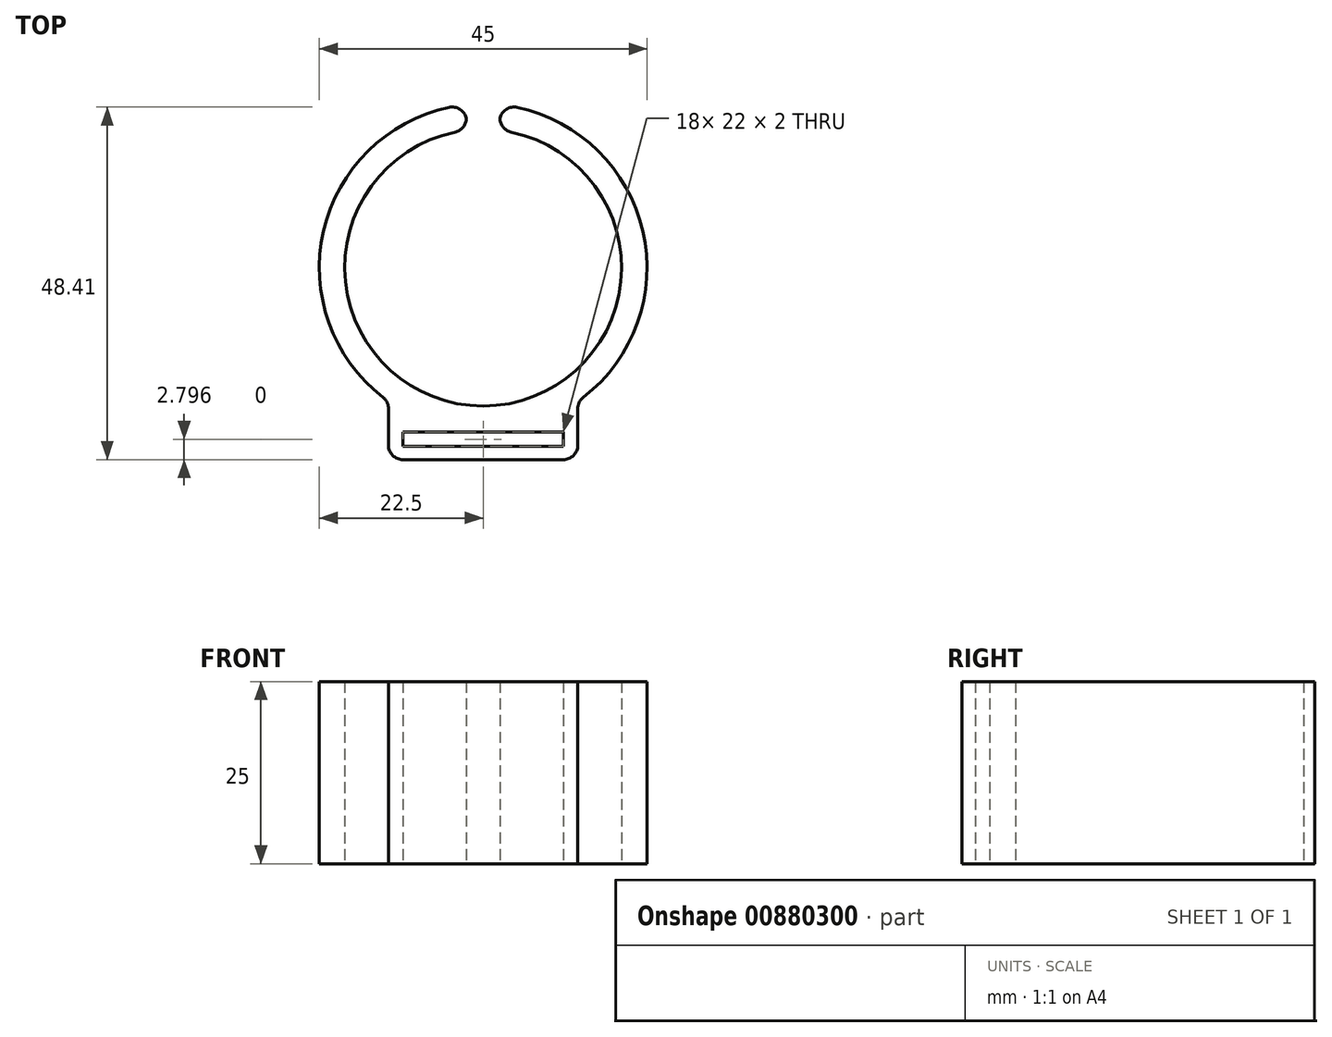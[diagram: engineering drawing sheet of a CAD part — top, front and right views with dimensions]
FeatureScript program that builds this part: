
annotation { "Feature Type Name" : "Feature", "Feature Type Description" : "" }
export const myFeature = defineFeature(function(context is Context, id is Id, definition is map)
    precondition{}
    {
        {
            var Q0;
            Q0=qCreatedBy(makeId("Top.planeOp"),FACE);
            var sketch = newSketch(context, id + "F0", { "sketchPlane" : qUnion([Q0])});
            skCircle(sketch, "E0", {"center": v(0, 0) * mm, "radius": 19 * mm});
            skCircle(sketch, "E1", {"center": v(0, 0) * mm, "radius": 22.5 * mm});
            skLineSegment(sketch, "E2", {"start": v(0, 0) * mm, "end": v(-2.5, 22.36) * mm});
            skLineSegment(sketch, "E3", {"start": v(0, 0) * mm, "end": v(2.5, 22.36) * mm});
            skLineSegment(sketch, "E4.bottom", {"start": v(-13, -18.36) * mm, "end": v(13, -18.36) * mm});
            skLineSegment(sketch, "E4.top", {"start": v(-13, -26.36) * mm, "end": v(13, -26.36) * mm});
            skLineSegment(sketch, "E4.left", {"start": v(-13, -18.36) * mm, "end": v(-13, -26.36) * mm});
            skLineSegment(sketch, "E4.right", {"start": v(13, -18.36) * mm, "end": v(13, -26.36) * mm});
            skLineSegment(sketch, "E5.bottom", {"start": v(-11, -22.56) * mm, "end": v(11, -22.56) * mm});
            skLineSegment(sketch, "E5.top", {"start": v(-11, -24.56) * mm, "end": v(11, -24.56) * mm});
            skLineSegment(sketch, "E5.left", {"start": v(-11, -22.56) * mm, "end": v(-11, -24.56) * mm});
            skLineSegment(sketch, "E5.right", {"start": v(11, -22.56) * mm, "end": v(11, -24.56) * mm});
            skSolve(sketch);
        }
        {
            var Q0;
            {var subQ0=sQuery(id+"F0.wireOp",EDGE,"E2");var subQ1=sQuery(id+"F0.wireOp",EDGE,"E0");var subQ2=makeQuery(id+"F0.imprint","INTERSECT",VERTEX,{"derivedFrom":[subQ1,subQ0]});Q0=makeQuery(id+"F0.imprint","IMPRINT",FACE,{"disambiguationData":[TD([[makeQuery(id+"F0.imprint","IMPRINT",EDGE,{"disambiguationData":[TD([[subQ2,-1.0]])],"derivedFrom":subQ1}),-1.0]])]});}
            var Q1;
            {var subQ0=sQuery(id+"F0.wireOp",EDGE,"E3");var subQ1=sQuery(id+"F0.wireOp",EDGE,"E0");var subQ2=makeQuery(id+"F0.imprint","INTERSECT",VERTEX,{"derivedFrom":[subQ1,subQ0]});Q1=makeQuery(id+"F0.imprint","IMPRINT",FACE,{"disambiguationData":[TD([[makeQuery(id+"F0.imprint","IMPRINT",EDGE,{"disambiguationData":[TD([[subQ2,1.0]])],"derivedFrom":subQ1}),-1.0]])]});}
            var Q2;
            {var subQ0=sQuery(id+"F0.wireOp",EDGE,"E4.bottom");var subQ1=sQuery(id+"F0.wireOp",EDGE,"E0");var subQ2=makeQuery(id+"F0.imprint","INTERSECT",VERTEX,{"disambiguationData":[OD(0.0)],"derivedFrom":[subQ1,subQ0]});Q2=makeQuery(id+"F0.imprint","IMPRINT",FACE,{"disambiguationData":[TD([[makeQuery(id+"F0.imprint","IMPRINT",EDGE,{"disambiguationData":[TD([[subQ2,-1.0]])],"derivedFrom":subQ1}),-1.0]])]});}
            var Q3;
            Q3=makeQuery(id+"F0.imprint","IMPRINT",FACE,{"disambiguationData":[TD([[makeQuery(id+"F0.imprint","IMPRINT",EDGE,{"derivedFrom":sQuery(id+"F0.wireOp",EDGE,"E4.top")}),1.0]])]});
            extrude(context, id + "F1", {"entities" : qUnion([Q0, Q1, Q2, Q3]), "depth" : 25 * mm, "offsetDistance" : 25 * mm});
        }
        {
            var Q0;
            Q0=makeQuery(id+"F1.opExtrude","SWEPT_EDGE",EDGE,{"disambiguationData":[OSD([sQuery(id+"F0.wireOp",EDGE,"E1"),sQuery(id+"F0.wireOp",EDGE,"E2")])]});
            var Q1;
            Q1=makeQuery(id+"F1.opExtrude","SWEPT_EDGE",EDGE,{"disambiguationData":[OSD([sQuery(id+"F0.wireOp",EDGE,"E1"),sQuery(id+"F0.wireOp",EDGE,"E3")])]});
            var Q2;
            Q2=makeQuery(id+"F1.opExtrude","SWEPT_EDGE",EDGE,{"disambiguationData":[OSD([sQuery(id+"F0.wireOp",EDGE,"E0"),sQuery(id+"F0.wireOp",EDGE,"E2")])]});
            var Q3;
            Q3=makeQuery(id+"F1.opExtrude","SWEPT_EDGE",EDGE,{"disambiguationData":[OSD([sQuery(id+"F0.wireOp",EDGE,"E0"),sQuery(id+"F0.wireOp",EDGE,"E3")])]});
            var Q4;
            Q4=makeQuery(id+"F1.opExtrude","SWEPT_EDGE",EDGE,{"disambiguationData":[OSD([sQuery(id+"F0.wireOp",EDGE,"E1"),sQuery(id+"F0.wireOp",EDGE,"E4.bottom"),sQuery(id+"F0.wireOp",EDGE,"E4.left")])]});
            var Q5;
            Q5=makeQuery(id+"F1.opExtrude","SWEPT_EDGE",EDGE,{"disambiguationData":[OSD([sQuery(id+"F0.wireOp",EDGE,"E1"),sQuery(id+"F0.wireOp",EDGE,"E4.bottom"),sQuery(id+"F0.wireOp",EDGE,"E4.right")])]});
            var Q6;
            Q6=makeQuery(id+"F1.opExtrude","SWEPT_EDGE",EDGE,{"disambiguationData":[OSD([sQuery(id+"F0.wireOp",EDGE,"E4.top"),sQuery(id+"F0.wireOp",EDGE,"E4.right")])]});
            var Q7;
            Q7=makeQuery(id+"F1.opExtrude","SWEPT_EDGE",EDGE,{"disambiguationData":[OSD([sQuery(id+"F0.wireOp",EDGE,"E4.top"),sQuery(id+"F0.wireOp",EDGE,"E4.left")])]});
            fillet(context, id + "F2", {"entities" : qUnion([Q0, Q1, Q2, Q3, Q4, Q5, Q6, Q7]), "radius" : 2 * mm, "tangentPropagation" : true, "allowEdgeOverflow" : false});
        }
    });
